# Revit family: Abstandswinkel E
name_source: partatom
category: HLS-Bauteile
revit_build: Autodesk Revit 2017 (Build: 20190507_1515(x64)
units: mm (PartAtom-declared; Revit-internal decimal feet)

## family parameters
Arbeitsebenenbasiert = Ja
Beim Laden mit Abzugskörper schneiden = Nein
Bemaßung runder Anschluss = Durchmesser verwenden
Gemeinsam genutzt = Ja
Immer vertikal = Nein
Raumberechnungspunkt = Nein
Teiletyp = Normal

## types (10) — shared parameters
B = 35 mm  [stored 0.114829 ft]
Firma = MEFA Befestigungs- und Montagesysteme GmbH
Vorgabe-Ansicht = 1219 mm

## per-type parameters (varying)
| type | Artikelnummer | Breite Schenkel | EAN | Fabrikat | Gewicht | Gewicht pro Bauteil | Kurztext1 | Kurztext2 | L1 | Langloch | Lochdurchmesser | Länge | Länge Schenkel | Material | Materialname | Mengeneinheit | Oberflaeche | Stärke Material | vpe |
| Abstandswinkel E  L= 25 | 0630268 | 35 mm  [stored 0.114829 ft] | 4250928415592 | MEFA | 0.07 kg | 0.07 kg | Abstandswinkel einfach | Länge 25 mm Langloch 10,5 x 25 mm | 25 mm  [stored 0.082021 ft] | 10,5 x 25 mm | 10.5 mm | 25 mm  [stored 0.082021 ft] | 42 mm  [stored 0.137795 ft] | Stahl | S235 | St | galvanisch verzinkt | 4 mm  [stored 0.0131234 ft] | 1 St |
| Abstandswinkel E  L= 30 | 0630306 | 35 mm  [stored 0.114829 ft] | 4250928415608 | MEFA | 0.08 kg | 0.08 kg | Abstandswinkel einfach | Länge 30 mm Langloch 10,5 x 25 mm | 30 mm  [stored 0.0984252 ft] | 10,5 x 25 mm | 10.5 mm | 30 mm  [stored 0.0984252 ft] | 42 mm  [stored 0.137795 ft] | Stahl | S235 | St | galvanisch verzinkt | 4 mm  [stored 0.0131234 ft] | 1 St |
| Abstandswinkel E  L= 35 | 0630357 | 35 mm  [stored 0.114829 ft] | 4250928415615 | MEFA | 0.08 kg | 0.08 kg | Abstandswinkel einfach | Länge 35 mm Langloch 10,5 x 25 mm | 35 mm  [stored 0.114829 ft] | 10,5 x 25 mm | 10.5 mm | 35 mm  [stored 0.114829 ft] | 42 mm  [stored 0.137795 ft] | Stahl | S235 | St | galvanisch verzinkt | 4 mm  [stored 0.0131234 ft] | 1 St |
| Abstandswinkel E  L= 40 | 0630403 | 35 mm  [stored 0.114829 ft] | 4250928415622 | MEFA | 0.09 kg | 0.09 kg | Abstandswinkel einfach | Länge 40 mm Langloch 10,5 x 25 mm | 40 mm  [stored 0.131234 ft] | 10,5 x 25 mm | 10.5 mm | 40 mm  [stored 0.131234 ft] | 42 mm  [stored 0.137795 ft] | Stahl | S235 | St | galvanisch verzinkt | 4 mm  [stored 0.0131234 ft] | 1 St |
| Abstandswinkel E  L= 50 | 0630500 | 35 mm  [stored 0.114829 ft] | 4250928415639 | MEFA | 0.10 kg | 0.10 kg | Abstandswinkel einfach | Länge 50 mm Langloch 10,5 x 25 mm | 50 mm  [stored 0.164042 ft] | 10,5 x 25 mm | 10.5 mm | 50 mm  [stored 0.164042 ft] | 42 mm  [stored 0.137795 ft] | Stahl | S235 | St | galvanisch verzinkt | 4 mm  [stored 0.0131234 ft] | 1 St |
| Abstandswinkel E  L= 60 | 0630608 | 35 mm  [stored 0.114829 ft] | 4250928415646 | MEFA | 0.11 kg | 0.11 kg | Abstandswinkel einfach | Länge 60 mm Langloch 10,5 x 25 mm | 60 mm  [stored 0.19685 ft] | 10,5 x 25 mm | 10.5 mm | 60 mm  [stored 0.19685 ft] | 42 mm  [stored 0.137795 ft] | Stahl | S235 | St | galvanisch verzinkt | 4 mm  [stored 0.0131234 ft] | 1 St |
| Abstandswinkel E  L= 70 | 0630705 | 35 mm  [stored 0.114829 ft] | 4250928415653 | MEFA | 0.12 kg | 0.12 kg | Abstandswinkel einfach | Länge 70 mm Langloch 10,5 x 25 mm | 70 mm  [stored 0.229659 ft] | 10,5 x 25 mm | 10.5 mm | 70 mm  [stored 0.229659 ft] | 42 mm  [stored 0.137795 ft] | Stahl | S235 | St | galvanisch verzinkt | 4 mm  [stored 0.0131234 ft] | 1 St |
| Abstandswinkel E  L= 80 | 0630802 | 0 mm  [stored 0 ft] |  |  | 0.00 kg | 0.00 kg |  |  | 80 mm  [stored 0.262467 ft] |  |  | 0 mm  [stored 0 ft] | 0 mm  [stored 0 ft] |  |  |  |  | 0 mm  [stored 0 ft] |  |
| Abstandswinkel E  L= 90 | 0630918 | 35 mm  [stored 0.114829 ft] | 4250928415677 | MEFA | 0.14 kg | 0.14 kg | Abstandswinkel einfach | Länge 90 mm Langloch 10,5 x 25 mm | 90 mm  [stored 0.295276 ft] | 10,5 x 25 mm | 10.5 mm | 90 mm  [stored 0.295276 ft] | 42 mm  [stored 0.137795 ft] | Stahl | S235 | St | galvanisch verzinkt | 4 mm  [stored 0.0131234 ft] | 1 St |
| Abstandswinkel E  L=100 | 0631000 | 35 mm  [stored 0.114829 ft] | 4250928415684 | MEFA | 0.15 kg | 0.15 kg | Abstandswinkel einfach | Länge 100 mm Langloch 10,5 x 25 mm | 100 mm  [stored 0.328084 ft] | 10,5 x 25 mm | 10.5 mm | 100 mm  [stored 0.328084 ft] | 42 mm  [stored 0.137795 ft] | Stahl | S235 | St | galvanisch verzinkt | 4 mm  [stored 0.0131234 ft] | 1 St |

note: [stored X ft] marks values corroborated as IEEE doubles in the binary element streams (Revit-internal decimal feet)
